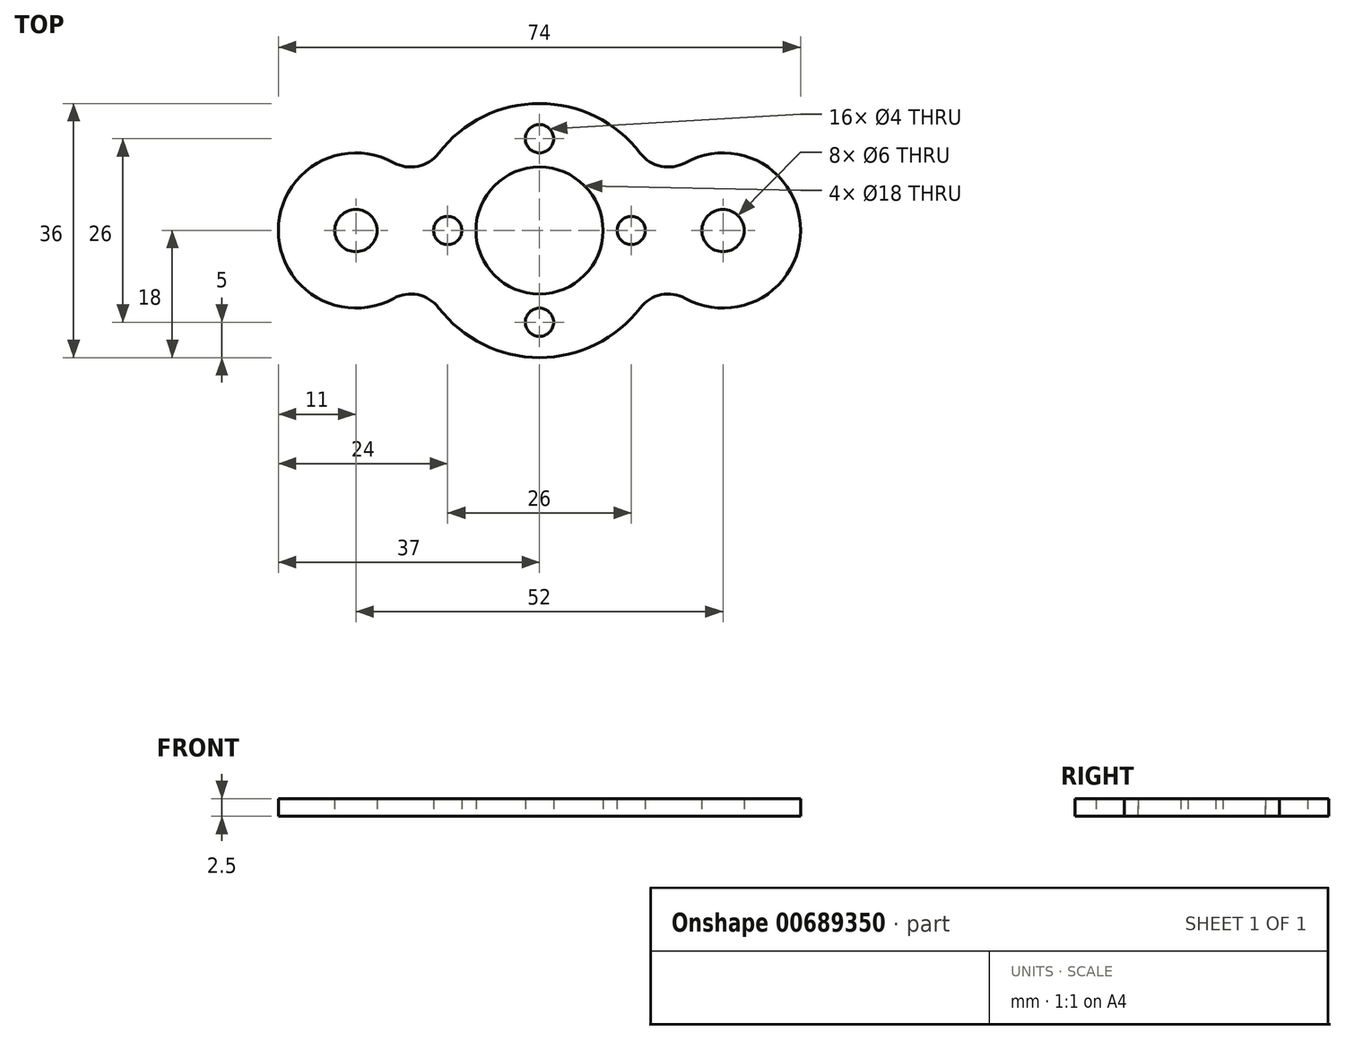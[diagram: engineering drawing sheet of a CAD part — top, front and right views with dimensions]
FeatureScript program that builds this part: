
annotation { "Feature Type Name" : "Feature", "Feature Type Description" : "" }
export const myFeature = defineFeature(function(context is Context, id is Id, definition is map)
    precondition{}
    {
        {
            var Q0;
            Q0=qCreatedBy(makeId("Top.planeOp"),FACE);
            var sketch = newSketch(context, id + "F0", { "sketchPlane" : qUnion([Q0])});
            skCircle(sketch, "E0", {"center": v(0, 0) * mm, "radius": 18 * mm});
            skCircle(sketch, "E1", {"center": v(26, 0) * mm, "radius": 11 * mm});
            skCircle(sketch, "E2", {"center": v(-26, 0) * mm, "radius": 11 * mm});
            skCircle(sketch, "E3", {"center": v(-26, 0) * mm, "radius": 3 * mm});
            skCircle(sketch, "E4", {"center": v(26, 0) * mm, "radius": 3 * mm});
            skCircle(sketch, "E5", {"center": v(0, 0) * mm, "radius": 9 * mm});
            skCircle(sketch, "E6", {"center": v(0, 13) * mm, "radius": 2 * mm});
            skCircle(sketch, "E7", {"center": v(13, 0) * mm, "radius": 2 * mm});
            skCircle(sketch, "E8", {"center": v(0, -13) * mm, "radius": 2 * mm});
            skCircle(sketch, "E9", {"center": v(-13, 0) * mm, "radius": 2 * mm});
            skSolve(sketch);
        }
        {
            var Q0;
            Q0 = qSketchRegion(id + "F0", true);
            extrude(context, id + "F1", {"entities" : qUnion([Q0]), "depth" : 2.5 * mm, "offsetDistance" : 25 * mm});
        }
        {
            var Q0;
            {var subQ0=sQuery(id+"F0.wireOp",EDGE,"E1");var subQ1=sQuery(id+"F0.wireOp",EDGE,"E0");Q0=makeQuery(id+"F1.opExtrude","SWEPT_EDGE",EDGE,{"disambiguationData":[OSD([subQ1,subQ0]),TDD([makeQuery(id+"F0.imprint","INTERSECT",VERTEX,{"disambiguationData":[OD(0.0)],"derivedFrom":[subQ1,subQ0]})])]});}
            var Q1;
            {var subQ0=sQuery(id+"F0.wireOp",EDGE,"E2");var subQ1=sQuery(id+"F0.wireOp",EDGE,"E0");Q1=makeQuery(id+"F1.opExtrude","SWEPT_EDGE",EDGE,{"disambiguationData":[OSD([subQ1,subQ0]),TDD([makeQuery(id+"F0.imprint","INTERSECT",VERTEX,{"disambiguationData":[OD(0.0)],"derivedFrom":[subQ1,subQ0]})])]});}
            var Q2;
            {var subQ0=sQuery(id+"F0.wireOp",EDGE,"E1");var subQ1=sQuery(id+"F0.wireOp",EDGE,"E0");Q2=makeQuery(id+"F1.opExtrude","SWEPT_EDGE",EDGE,{"disambiguationData":[OSD([subQ1,subQ0]),TDD([makeQuery(id+"F0.imprint","INTERSECT",VERTEX,{"disambiguationData":[OD(1.0)],"derivedFrom":[subQ1,subQ0]})])]});}
            var Q3;
            {var subQ0=sQuery(id+"F0.wireOp",EDGE,"E2");var subQ1=sQuery(id+"F0.wireOp",EDGE,"E0");Q3=makeQuery(id+"F1.opExtrude","SWEPT_EDGE",EDGE,{"disambiguationData":[OSD([subQ1,subQ0]),TDD([makeQuery(id+"F0.imprint","INTERSECT",VERTEX,{"disambiguationData":[OD(1.0)],"derivedFrom":[subQ1,subQ0]})])]});}
            fillet(context, id + "F2", {"entities" : qUnion([Q0, Q1, Q2, Q3]), "radius" : 5 * mm, "tangentPropagation" : true, "allowEdgeOverflow" : false});
        }
    });
